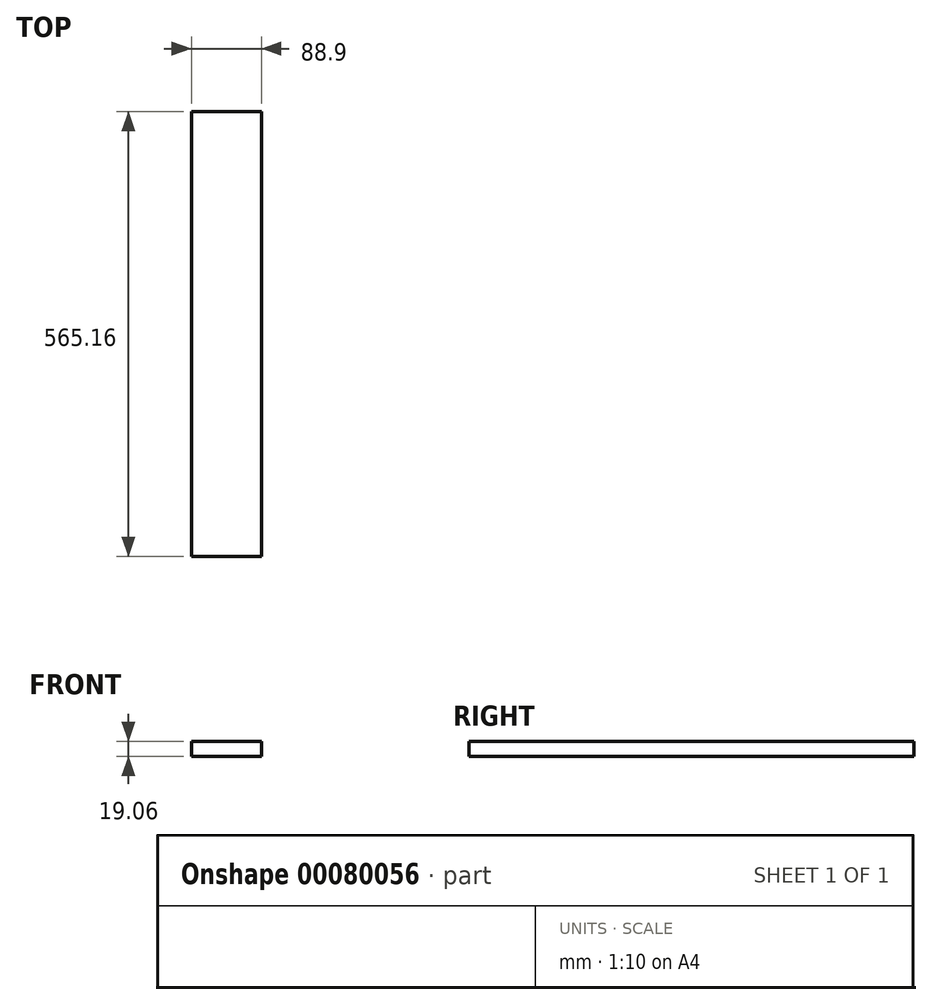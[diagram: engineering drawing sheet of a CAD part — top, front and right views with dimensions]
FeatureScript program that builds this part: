
annotation { "Feature Type Name" : "Feature", "Feature Type Description" : "" }
export const myFeature = defineFeature(function(context is Context, id is Id, definition is map)
    precondition{}
    {
        {
            var Q0;
            Q0=qCreatedBy(makeId("Front.planeOp"),FACE);
            var sketch = newSketch(context, id + "F0", { "sketchPlane" : qUnion([Q0])});
            skLineSegment(sketch, "E0.bottom", {"start": v(-44.45, 9.52) * mm, "end": v(44.45, 9.52) * mm});
            skLineSegment(sketch, "E0.top", {"start": v(-44.45, -9.52) * mm, "end": v(44.45, -9.52) * mm});
            skLineSegment(sketch, "E0.left", {"start": v(-44.45, 9.52) * mm, "end": v(-44.45, -9.52) * mm});
            skLineSegment(sketch, "E0.right", {"start": v(44.45, 9.52) * mm, "end": v(44.45, -9.52) * mm});
            skPoint(sketch, "E0.middle", {"position": v(0, 0) * mm});
            skSolve(sketch);
        }
        {
            var Q0;
            Q0=makeQuery(id+"F0.imprint","IMPRINT",FACE,{"disambiguationData":[TD([[makeQuery(id+"F0.imprint","IMPRINT",EDGE,{"derivedFrom":sQuery(id+"F0.wireOp",EDGE,"E0.bottom")}),-1.0]])]});
            extrude(context, id + "F1", {"entities" : qUnion([Q0]), "endBound" : BoundingType.SYMMETRIC, "depth" : 565.15 * mm});
        }
    });
